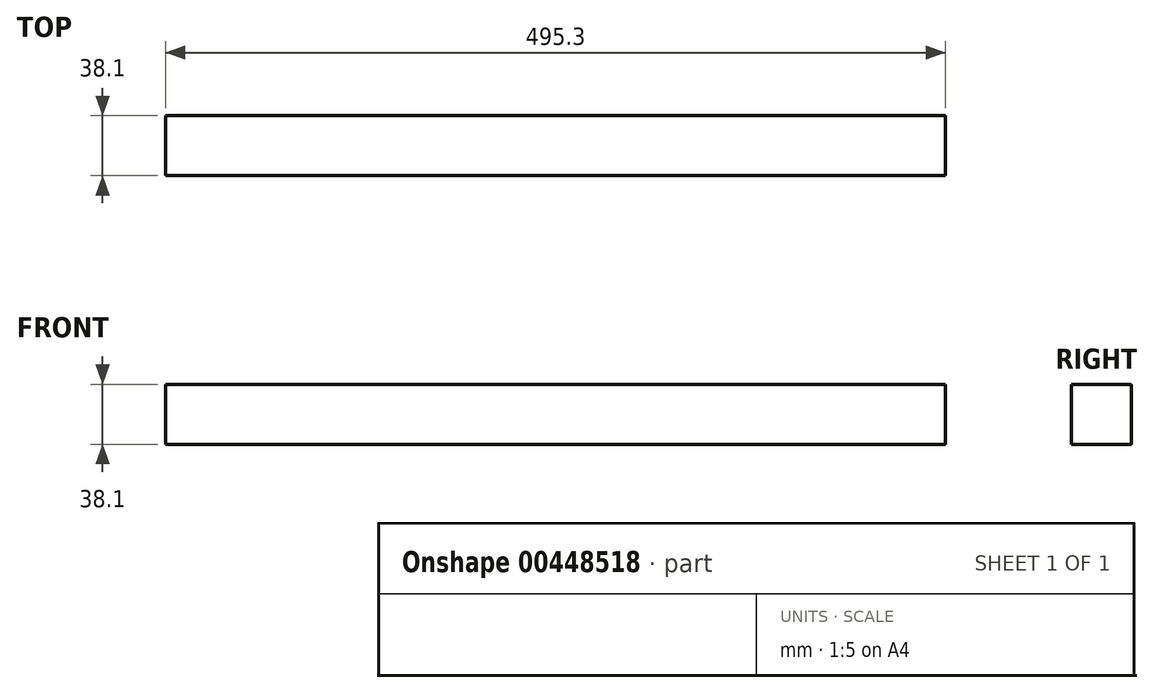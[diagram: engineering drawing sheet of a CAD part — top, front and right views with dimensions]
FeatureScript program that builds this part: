
annotation { "Feature Type Name" : "Feature", "Feature Type Description" : "" }
export const myFeature = defineFeature(function(context is Context, id is Id, definition is map)
    precondition{}
    {
        {
            var Q0;
            Q0=qCreatedBy(makeId("Front.planeOp"),FACE);
            var sketch = newSketch(context, id + "F0", { "sketchPlane" : qUnion([Q0])});
            skLineSegment(sketch, "E0.bottom", {"start": v(0, 0) * mm, "end": v(495.3, 0) * mm});
            skLineSegment(sketch, "E0.top", {"start": v(0, -38.1) * mm, "end": v(495.3, -38.1) * mm});
            skLineSegment(sketch, "E0.right", {"start": v(495.3, 0) * mm, "end": v(495.3, -38.1) * mm});
            skLineSegment(sketch, "E1", {"start": v(0, -38.1) * mm, "end": v(0, 0) * mm});
            skSolve(sketch);
        }
        {
            var Q0;
            Q0=makeQuery(id+"F0.imprint","IMPRINT",FACE,{"disambiguationData":[TD([[makeQuery(id+"F0.imprint","IMPRINT",EDGE,{"derivedFrom":sQuery(id+"F0.wireOp",EDGE,"E0.bottom")}),-1.0]])]});
            extrude(context, id + "F1", {"entities" : qUnion([Q0]), "depth" : 38.1 * mm});
        }
    });
